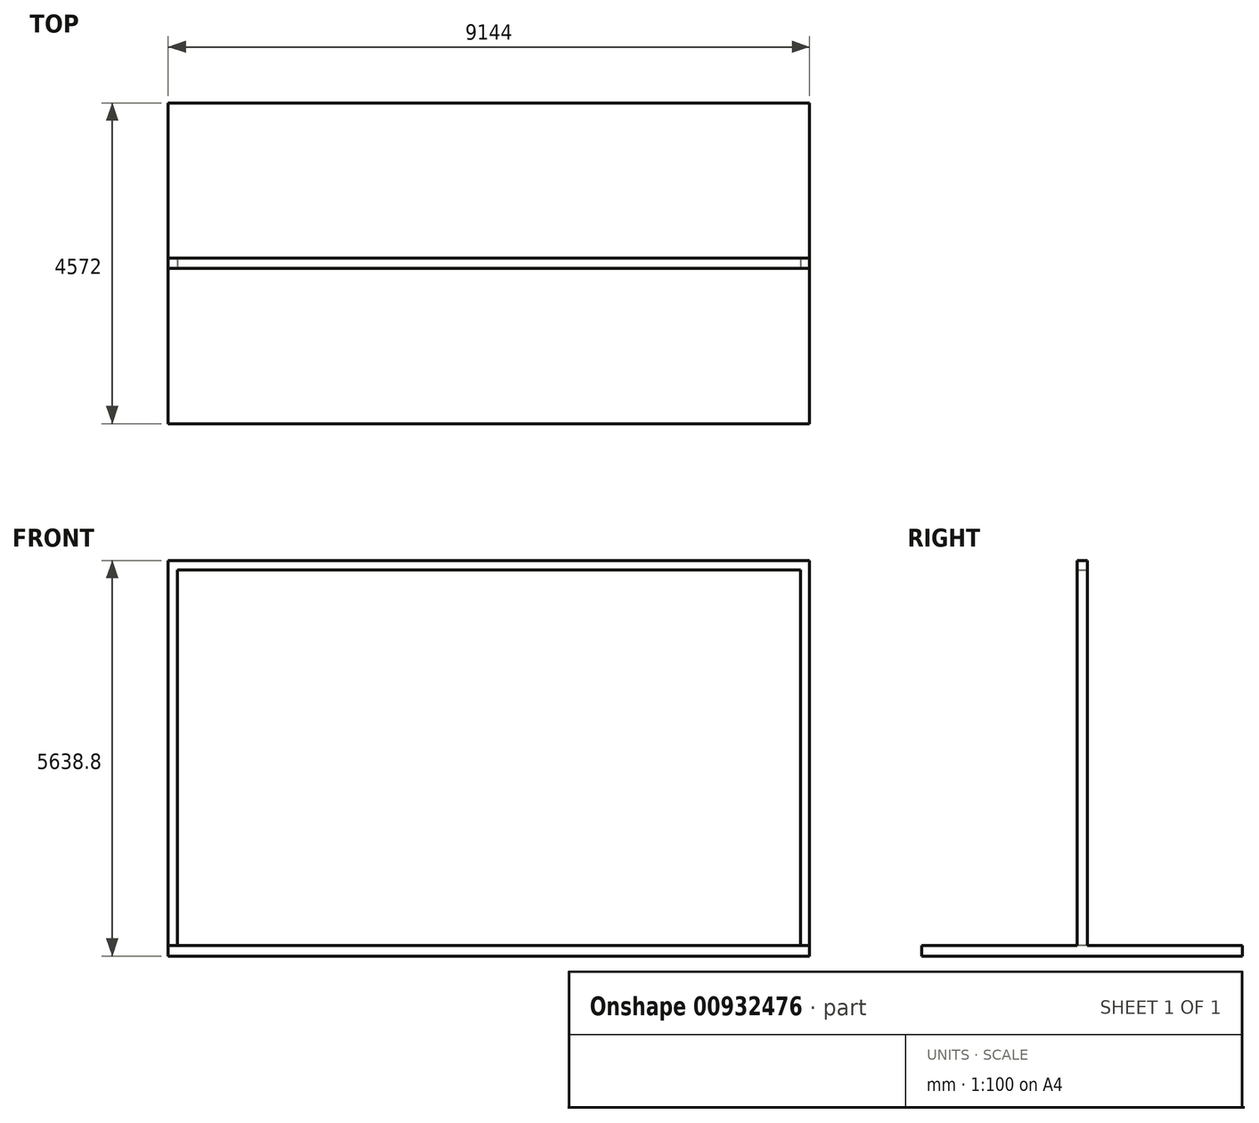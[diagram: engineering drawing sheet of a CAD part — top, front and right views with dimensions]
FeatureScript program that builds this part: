
annotation { "Feature Type Name" : "Feature", "Feature Type Description" : "" }
export const myFeature = defineFeature(function(context is Context, id is Id, definition is map)
    precondition{}
    {
        {
            var Q0;
            Q0=qCreatedBy(makeId("Top.planeOp"),FACE);
            var sketch = newSketch(context, id + "F0", { "sketchPlane" : qUnion([Q0])});
            skLineSegment(sketch, "E0.bottom", {"start": v(4572, 2286) * mm, "end": v(-4572, 2286) * mm});
            skLineSegment(sketch, "E0.top", {"start": v(4572, -2286) * mm, "end": v(-4572, -2286) * mm});
            skLineSegment(sketch, "E0.left", {"start": v(4572, 2286) * mm, "end": v(4572, -2286) * mm});
            skLineSegment(sketch, "E0.right", {"start": v(-4572, 2286) * mm, "end": v(-4572, -2286) * mm});
            skPoint(sketch, "E0.middle", {"position": v(0, 0) * mm});
            skSolve(sketch);
        }
        {
            var Q0;
            Q0 = qSketchRegion(id + "F0", true);
            var Q1;
            Q1=makeQuery(id+"F0.imprint","IMPRINT",FACE,{"disambiguationData":[TD([[makeQuery(id+"F0.imprint","IMPRINT",EDGE,{"derivedFrom":sQuery(id+"F0.wireOp",EDGE,"E0.bottom")}),1.0]])]});
            extrude(context, id + "F1", {"entities" : qUnion([Q0, Q1]), "depth" : 152.4 * mm, "offsetDistance" : 25.4 * mm});
        }
        {
            var Q0;
            Q0=makeQuery(id+"F1.opExtrude","CAP_FACE",FACE,{"disambiguationData":[OSD([sQuery(id+"F0.wireOp",EDGE,"E0.bottom"),sQuery(id+"F0.wireOp",EDGE,"E0.top"),sQuery(id+"F0.wireOp",EDGE,"E0.left"),sQuery(id+"F0.wireOp",EDGE,"E0.right")])],"isStart":false});
            var sketch = newSketch(context, id + "F2", { "sketchPlane" : qUnion([Q0])});
            skLineSegment(sketch, "E1", {"start": v(-4572, 0) * mm, "end": v(4572, 0) * mm, "construction": true});
            skLineSegment(sketch, "E2", {"start": v(3962.4, 2286) * mm, "end": v(3962.4, -2286) * mm, "construction": true});
            skLineSegment(sketch, "E3", {"start": v(-3962.4, 2286) * mm, "end": v(-3962.4, -2286) * mm, "construction": true});
            skLineSegment(sketch, "E4", {"start": v(304.8, 2286) * mm, "end": v(304.8, -2286) * mm, "construction": true});
            skLineSegment(sketch, "E5", {"start": v(914.4, 2286) * mm, "end": v(914.4, -2286) * mm, "construction": true});
            skLineSegment(sketch, "E6", {"start": v(1524, 2286) * mm, "end": v(1524, -2286) * mm, "construction": true});
            skLineSegment(sketch, "E7", {"start": v(2133.6, 2286) * mm, "end": v(2133.6, -2286) * mm, "construction": true});
            skLineSegment(sketch, "E8", {"start": v(2743.2, 2286) * mm, "end": v(2743.2, -2286) * mm, "construction": true});
            skLineSegment(sketch, "E9", {"start": v(3352.8, 2286) * mm, "end": v(3352.8, -2286) * mm, "construction": true});
            skLineSegment(sketch, "E10.MirrorCS", {"start": v(-304.8, 2286) * mm, "end": v(-304.8, -2286) * mm, "construction": true});
            skLineSegment(sketch, "E11.MirrorCS", {"start": v(-914.4, 2286) * mm, "end": v(-914.4, -2286) * mm, "construction": true});
            skLineSegment(sketch, "E12.MirrorCS", {"start": v(-1524, 2286) * mm, "end": v(-1524, -2286) * mm, "construction": true});
            skLineSegment(sketch, "E13.MirrorCS", {"start": v(-2133.6, 2286) * mm, "end": v(-2133.6, -2286) * mm, "construction": true});
            skLineSegment(sketch, "E14.MirrorCS", {"start": v(-2743.2, 2286) * mm, "end": v(-2743.2, -2286) * mm, "construction": true});
            skLineSegment(sketch, "E15.MirrorCS", {"start": v(-3352.8, 2286) * mm, "end": v(-3352.8, -2286) * mm, "construction": true});
            skLineSegment(sketch, "E16", {"start": v(-4572, 2082.8) * mm, "end": v(4572, 2082.8) * mm, "construction": true});
            skLineSegment(sketch, "E17", {"start": v(-4572, -2082.8) * mm, "end": v(4572, -2082.8) * mm, "construction": true});
            skLineSegment(sketch, "E18.bottom", {"start": v(-4443.04, 75.7) * mm, "end": v(-4700.96, 75.7) * mm});
            skLineSegment(sketch, "E18.top", {"start": v(-4443.04, -75.7) * mm, "end": v(-4700.96, -75.7) * mm});
            skLineSegment(sketch, "E18.left", {"start": v(-4443.04, 75.7) * mm, "end": v(-4443.04, -75.7) * mm});
            skLineSegment(sketch, "E18.right", {"start": v(-4700.96, 75.7) * mm, "end": v(-4700.96, -75.7) * mm});
            skPoint(sketch, "E18.middle", {"position": v(-4572, 0) * mm});
            skLineSegment(sketch, "E19.MirrorCS", {"start": v(4443.04, 75.7) * mm, "end": v(4443.04, -75.7) * mm});
            skLineSegment(sketch, "E20.MirrorCS", {"start": v(4443.04, 75.7) * mm, "end": v(4700.96, 75.7) * mm});
            skLineSegment(sketch, "E21.MirrorCS", {"start": v(4443.04, -75.7) * mm, "end": v(4700.96, -75.7) * mm});
            skLineSegment(sketch, "E22.MirrorCS", {"start": v(4700.96, 75.7) * mm, "end": v(4700.96, -75.7) * mm});
            skLineSegment(sketch, "E23", {"start": v(-4572, -2082.8) * mm, "end": v(4572, -2082.8) * mm});
            skLineSegment(sketch, "E24", {"start": v(-4572, 2082.8) * mm, "end": v(4572, 2082.8) * mm});
            skSolve(sketch);
        }
        {
            var Q0;
            {var subQ0=sQuery(id+"F2.wireOp",EDGE,"E18.left");Q0=makeQuery(id+"F2.imprint","IMPRINT",FACE,{"disambiguationData":[TD([[makeQuery(id+"F2.imprint","IMPRINT",EDGE,{"derivedFrom":subQ0}),-1.0]])]});}
            var Q1;
            {var subQ0=sQuery(id+"F2.wireOp",EDGE,"E19.MirrorCS");Q1=makeQuery(id+"F2.imprint","IMPRINT",FACE,{"disambiguationData":[TD([[makeQuery(id+"F2.imprint","IMPRINT",EDGE,{"derivedFrom":subQ0}),1.0]])]});}
            extrude(context, id + "F3", {"entities" : qUnion([Q0, Q1]), "operationType" : NewBodyOperationType.ADD, "depth" : 5486.4 * mm, "offsetDistance" : 25.4 * mm});
        }
        {
            var Q0;
            Q0=makeQuery(id+"F3.opExtrude","SWEPT_FACE",FACE,{"disambiguationData":[OSD([sQuery(id+"F2.wireOp",EDGE,"E18.left")])]});
            var sketch = newSketch(context, id + "F4", { "sketchPlane" : qUnion([Q0])});
            skLineSegment(sketch, "E25.bottom", {"start": v(-75.7, 5638.8) * mm, "end": v(75.7, 5638.8) * mm});
            skLineSegment(sketch, "E25.top", {"start": v(-75.7, 5501.85) * mm, "end": v(75.7, 5501.85) * mm});
            skLineSegment(sketch, "E25.left", {"start": v(-75.7, 5638.8) * mm, "end": v(-75.7, 5501.85) * mm});
            skLineSegment(sketch, "E25.right", {"start": v(75.7, 5638.8) * mm, "end": v(75.7, 5501.85) * mm});
            skSolve(sketch);
        }
        {
            var Q0;
            Q0 = qSketchRegion(id + "F4", true);
            extrude(context, id + "F5", {"entities" : qUnion([Q0]), "operationType" : NewBodyOperationType.ADD, "endBound" : BoundingType.UP_TO_NEXT, "depth" : 25.4 * mm, "offsetDistance" : 25.4 * mm});
        }
        {
            var Q0;
            Q0=makeQuery(id+"F1.opExtrude","CAP_EDGE",EDGE,{"disambiguationData":[OSD([sQuery(id+"F0.wireOp",EDGE,"E0.bottom")])],"isStart":false});
            var Q1;
            Q1=makeQuery(id+"F5.boolean.opBoolean","MERGE",EDGE,{"derivedFrom":[makeQuery(id+"F3.opExtrude","CAP_EDGE",EDGE,{"disambiguationData":[OSD([sQuery(id+"F2.wireOp",EDGE,"E18.bottom")])],"isStart":false}),makeQuery(id+"F3.opExtrude","CAP_EDGE",EDGE,{"disambiguationData":[OSD([sQuery(id+"F2.wireOp",EDGE,"E20.MirrorCS")])],"isStart":false}),makeQuery(id+"F5.opExtrude","SWEPT_EDGE",EDGE,{"disambiguationData":[OSD([sQuery(id+"F4.wireOp",EDGE,"E25.bottom"),sQuery(id+"F4.wireOp",EDGE,"E25.right")])]})]});
            loft(context, id + "F6", {"bodyType" : ToolBodyType.SURFACE, "wireProfilesArray" : [{ "wireProfileEntities" : qUnion([Q0]) }, { "wireProfileEntities" : qUnion([Q1]) }]});
        }
    });
